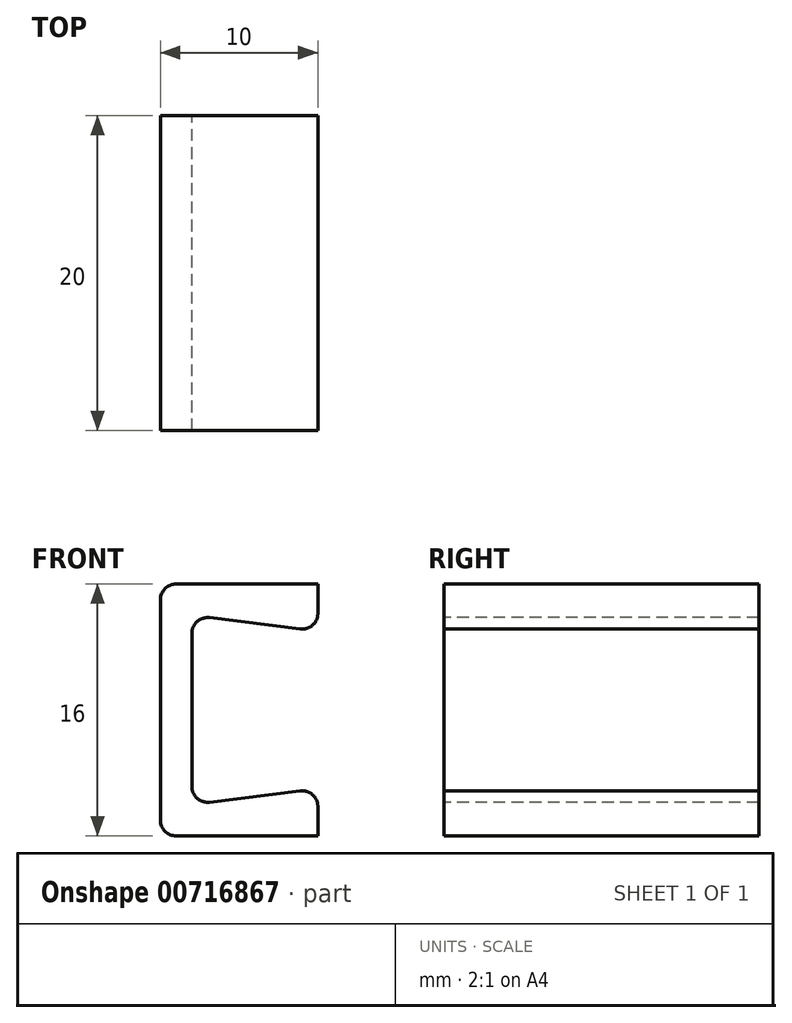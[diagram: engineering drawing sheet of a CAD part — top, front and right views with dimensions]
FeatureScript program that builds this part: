
annotation { "Feature Type Name" : "Feature", "Feature Type Description" : "" }
export const myFeature = defineFeature(function(context is Context, id is Id, definition is map)
    precondition{}
    {
        {
            var Q0;
            Q0=qCreatedBy(makeId("Front.planeOp"),FACE);
            var sketch = newSketch(context, id + "F0", { "sketchPlane" : qUnion([Q0])});
            skLineSegment(sketch, "E0", {"start": v(10, 16) * mm, "end": v(0, 16) * mm});
            skLineSegment(sketch, "E1", {"start": v(0, 16) * mm, "end": v(0, 0) * mm});
            skLineSegment(sketch, "E2", {"start": v(0, 0) * mm, "end": v(10, 0) * mm});
            skLineSegment(sketch, "E3", {"start": v(10, 0) * mm, "end": v(10, 3) * mm});
            skLineSegment(sketch, "E4", {"start": v(10, 3) * mm, "end": v(2, 2) * mm});
            skLineSegment(sketch, "E5", {"start": v(2, 2) * mm, "end": v(2, 14) * mm});
            skLineSegment(sketch, "E6", {"start": v(2, 14) * mm, "end": v(10, 13) * mm});
            skLineSegment(sketch, "E7", {"start": v(10, 13) * mm, "end": v(10, 16) * mm});
            skSolve(sketch);
        }
        {
            var Q0;
            Q0 = qSketchRegion(id + "F0", true);
            extrude(context, id + "F1", {"entities" : qUnion([Q0]), "depth" : 20 * mm, "offsetDistance" : 25 * mm});
        }
        {
            var Q0;
            Q0=makeQuery(id+"F1.opExtrude","SWEPT_EDGE",EDGE,{"disambiguationData":[OSD([sQuery(id+"F0.wireOp",EDGE,"E6"),sQuery(id+"F0.wireOp",EDGE,"E7")])]});
            var Q1;
            Q1=makeQuery(id+"F1.opExtrude","SWEPT_EDGE",EDGE,{"disambiguationData":[OSD([sQuery(id+"F0.wireOp",EDGE,"E3"),sQuery(id+"F0.wireOp",EDGE,"E4")])]});
            var Q2;
            Q2=makeQuery(id+"F1.opExtrude","SWEPT_EDGE",EDGE,{"disambiguationData":[OSD([sQuery(id+"F0.wireOp",EDGE,"E5"),sQuery(id+"F0.wireOp",EDGE,"E6")])]});
            var Q3;
            Q3=makeQuery(id+"F1.opExtrude","SWEPT_EDGE",EDGE,{"disambiguationData":[OSD([sQuery(id+"F0.wireOp",EDGE,"E4"),sQuery(id+"F0.wireOp",EDGE,"E5")])]});
            fillet(context, id + "F2", {"entities" : qUnion([Q0, Q1, Q2, Q3]), "radius" : 1 * mm, "tangentPropagation" : true, "allowEdgeOverflow" : false});
        }
        {
            var Q0;
            Q0=makeQuery(id+"F1.opExtrude","SWEPT_EDGE",EDGE,{"disambiguationData":[OSD([sQuery(id+"F0.wireOp",EDGE,"E1"),sQuery(id+"F0.wireOp",EDGE,"E2")])]});
            var Q1;
            Q1=makeQuery(id+"F1.opExtrude","SWEPT_EDGE",EDGE,{"disambiguationData":[OSD([sQuery(id+"F0.wireOp",EDGE,"E0"),sQuery(id+"F0.wireOp",EDGE,"E1")])]});
            fillet(context, id + "F3", {"entities" : qUnion([Q0, Q1]), "radius" : 1 * mm, "tangentPropagation" : true, "allowEdgeOverflow" : false});
        }
    });
